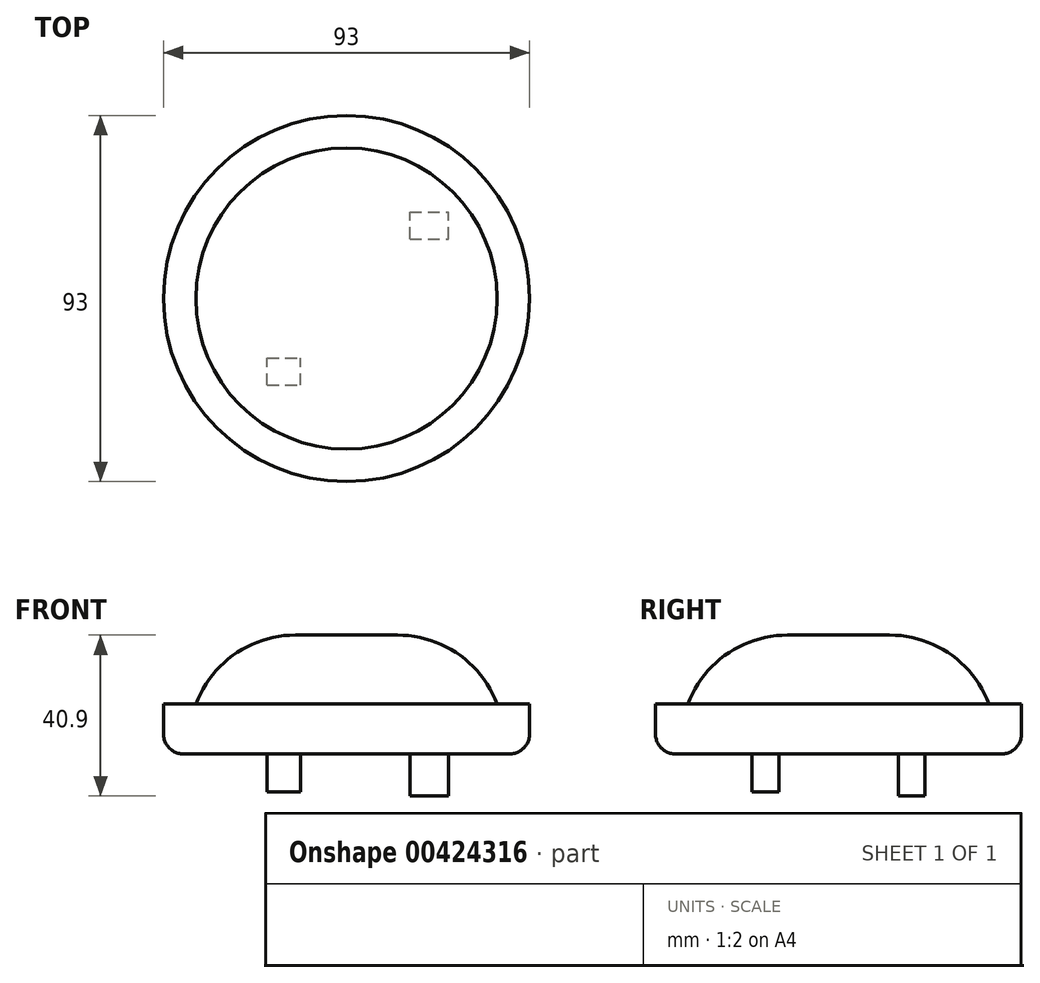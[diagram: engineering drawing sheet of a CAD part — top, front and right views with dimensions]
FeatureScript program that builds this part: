
annotation { "Feature Type Name" : "Feature", "Feature Type Description" : "" }
export const myFeature = defineFeature(function(context is Context, id is Id, definition is map)
    precondition{}
    {
        {
            var Q0;
            Q0=qCreatedBy(makeId("Top.planeOp"),FACE);
            var sketch = newSketch(context, id + "F0", { "sketchPlane" : qUnion([Q0])});
            skCircle(sketch, "E0", {"center": v(0, 0) * mm, "radius": 38.25 * mm});
            skSolve(sketch);
        }
        {
            var Q0;
            Q0=makeQuery(id+"F0.imprint","IMPRINT",FACE,{"disambiguationData":[TD([[makeQuery(id+"F0.imprint","IMPRINT",EDGE,{"derivedFrom":sQuery(id+"F0.wireOp",EDGE,"E0")}),1.0]])]});
            extrude(context, id + "F1", {"entities" : qUnion([Q0]), "depth" : 17.53 * mm});
        }
        {
            var Q0;
            Q0=makeQuery(id+"F1.opExtrude","CAP_FACE",FACE,{"disambiguationData":[OSD([sQuery(id+"F0.wireOp",EDGE,"E0")])],"isStart":false});
            fillet(context, id + "F2", {"entities" : qUnion([Q0]), "radius" : 26.98 * mm, "tangentPropagation" : true, "allowEdgeOverflow" : false});
        }
        {
            var Q0;
            Q0=makeQuery(id+"F1.opExtrude","CAP_FACE",FACE,{"disambiguationData":[OSD([sQuery(id+"F0.wireOp",EDGE,"E0")])],"isStart":true});
            var sketch = newSketch(context, id + "F3", { "sketchPlane" : qUnion([Q0])});
            skCircle(sketch, "E1", {"center": v(0, 0) * mm, "radius": 46.5 * mm});
            skSolve(sketch);
        }
        {
            var Q0;
            Q0 = qSketchRegion(id + "F3", true);
            extrude(context, id + "F4", {"entities" : qUnion([Q0]), "operationType" : NewBodyOperationType.ADD, "depth" : 12.7 * mm});
        }
        {
            var Q0;
            Q0=makeQuery(id+"F4.opExtrude","CAP_FACE",FACE,{"disambiguationData":[OSD([sQuery(id+"F3.wireOp",EDGE,"E1")])],"isStart":false});
            fillet(context, id + "F5", {"entities" : qUnion([Q0]), "radius" : 5.08 * mm, "tangentPropagation" : true, "allowEdgeOverflow" : false});
        }
        {
            var Q0;
            Q0=makeQuery(id+"F4.opExtrude","CAP_FACE",FACE,{"disambiguationData":[OSD([sQuery(id+"F3.wireOp",EDGE,"E1")])],"isStart":false});
            var sketch = newSketch(context, id + "F6", { "sketchPlane" : qUnion([Q0])});
            skLineSegment(sketch, "E2.bottom", {"start": v(-20.15, 22) * mm, "end": v(-11.7, 22) * mm});
            skLineSegment(sketch, "E2.top", {"start": v(-20.15, 15.1) * mm, "end": v(-11.7, 15.1) * mm});
            skLineSegment(sketch, "E2.left", {"start": v(-20.15, 22) * mm, "end": v(-20.15, 15.1) * mm});
            skLineSegment(sketch, "E2.right", {"start": v(-11.7, 22) * mm, "end": v(-11.7, 15.1) * mm});
            skSolve(sketch);
        }
        {
            var Q0;
            Q0=makeQuery(id+"F4.opExtrude","CAP_FACE",FACE,{"disambiguationData":[OSD([sQuery(id+"F3.wireOp",EDGE,"E1")])],"isStart":false});
            var sketch = newSketch(context, id + "F7", { "sketchPlane" : qUnion([Q0])});
            skLineSegment(sketch, "E3.bottom", {"start": v(16.09, -15.16) * mm, "end": v(25.87, -15.16) * mm});
            skLineSegment(sketch, "E3.top", {"start": v(16.09, -21.94) * mm, "end": v(25.87, -21.94) * mm});
            skLineSegment(sketch, "E3.left", {"start": v(16.09, -15.16) * mm, "end": v(16.09, -21.94) * mm});
            skLineSegment(sketch, "E3.right", {"start": v(25.87, -15.16) * mm, "end": v(25.87, -21.94) * mm});
            skSolve(sketch);
        }
        {
            var Q0;
            Q0=makeQuery(id+"F6.imprint","IMPRINT",FACE,{"disambiguationData":[TD([[makeQuery(id+"F6.imprint","IMPRINT",EDGE,{"derivedFrom":sQuery(id+"F6.wireOp",EDGE,"E2.bottom")}),-1.0]])]});
            extrude(context, id + "F8", {"entities" : qUnion([Q0]), "operationType" : NewBodyOperationType.ADD, "depth" : 9.65 * mm});
        }
        {
            var Q0;
            Q0=makeQuery(id+"F7.imprint","IMPRINT",FACE,{"disambiguationData":[TD([[makeQuery(id+"F7.imprint","IMPRINT",EDGE,{"derivedFrom":sQuery(id+"F7.wireOp",EDGE,"E3.bottom")}),-1.0]])]});
            extrude(context, id + "F9", {"entities" : qUnion([Q0]), "operationType" : NewBodyOperationType.ADD, "depth" : 10.67 * mm});
        }
    });
